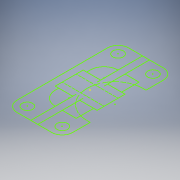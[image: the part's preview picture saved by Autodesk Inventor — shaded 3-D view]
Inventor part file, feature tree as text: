
AUTODESK INVENTOR PART (.ipt)
format: ipt  version: 2018 (Build 220112000, 112)  size: 111,104 bytes
history: native  units: in
note: dims shown in document units (in); Inventor stores cm internally (conversion verified against a paired STEP export)
features: sketch x3
ambient origin geometry x8: Origin, YZ Plane, XZ Plane, XY Plane, X Axis, Y Axis, Z Axis, Center Point
feature tree (3):
  sketch  "草图1"  dims[d41=3.1496in]
  sketch  "草图4"  dims[d45=1.5748in]
  sketch  "草图5"
